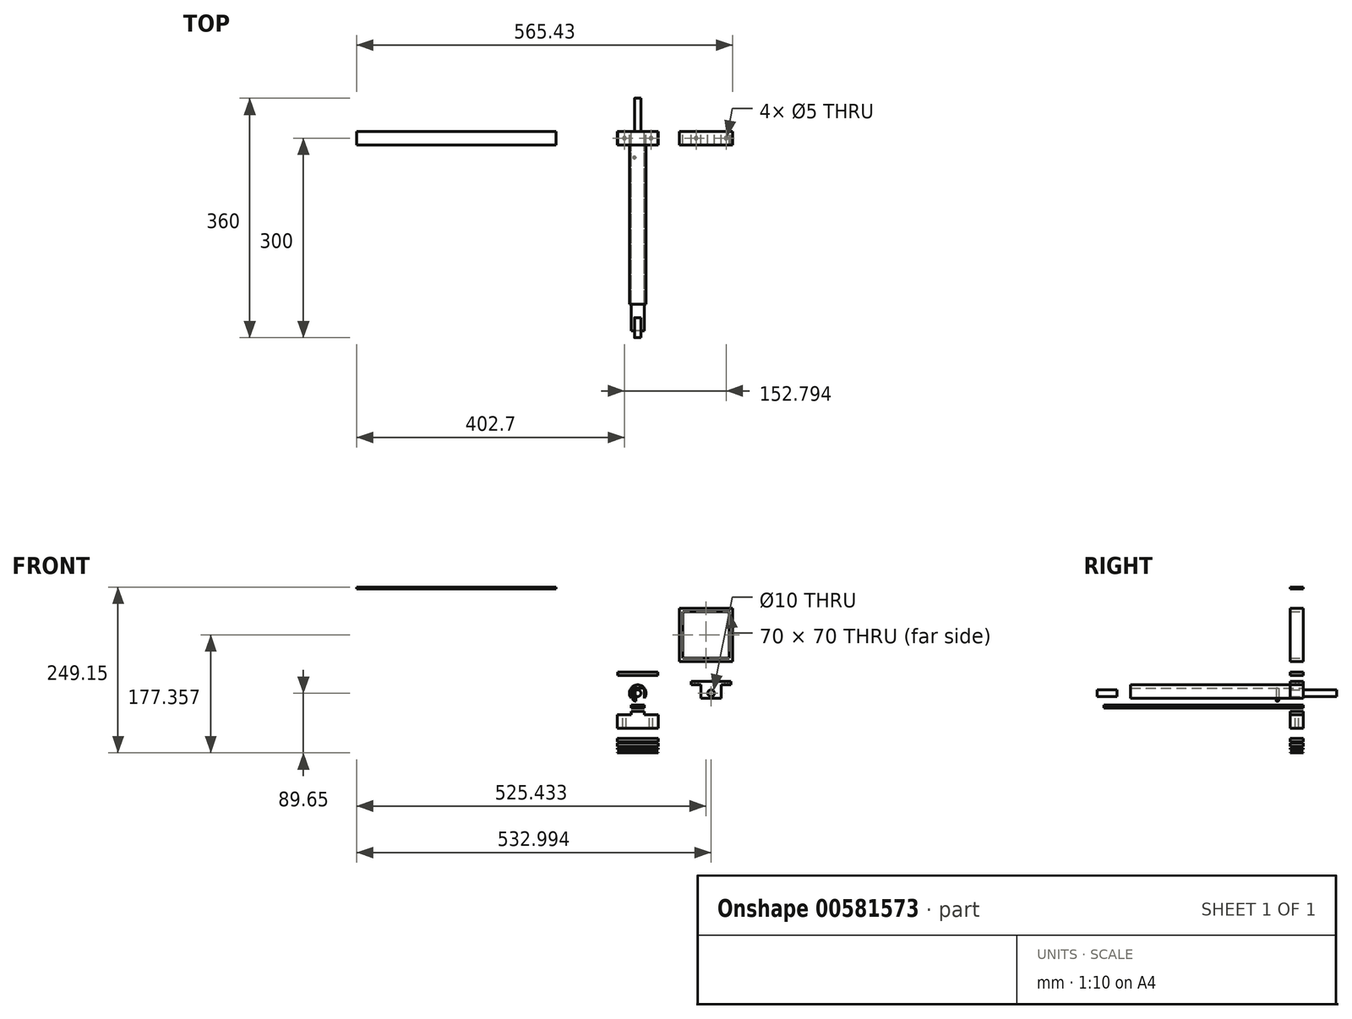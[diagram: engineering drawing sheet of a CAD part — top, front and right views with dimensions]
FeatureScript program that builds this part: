
annotation { "Feature Type Name" : "Feature", "Feature Type Description" : "" }
export const myFeature = defineFeature(function(context is Context, id is Id, definition is map)
    precondition{}
    {
        {
            var Q0;
            Q0=qCreatedBy(makeId("Front.planeOp"),FACE);
            var sketch = newSketch(context, id + "F0", { "sketchPlane" : qUnion([Q0])});
            skCircle(sketch, "E0", {"center": v(0, 0) * mm, "radius": 12.5 * mm});
            skCircle(sketch, "E1", {"center": v(110.3, 0) * mm, "radius": 5 * mm});
            skLineSegment(sketch, "E2.bottom", {"start": v(-30, 31.74) * mm, "end": v(30, 31.74) * mm});
            skLineSegment(sketch, "E2.top", {"start": v(-30, 26.74) * mm, "end": v(30, 26.74) * mm});
            skLineSegment(sketch, "E2.left", {"start": v(-30, 31.74) * mm, "end": v(-30, 26.74) * mm});
            skLineSegment(sketch, "E2.right", {"start": v(30, 31.74) * mm, "end": v(30, 26.74) * mm});
            skPoint(sketch, "E2.middle", {"position": v(0, 29.24) * mm});
            skLineSegment(sketch, "E3", {"start": v(110.3, 10) * mm, "end": v(110.3, -10) * mm, "construction": true});
            skCircle(sketch, "E4", {"center": v(110.3, 0) * mm, "radius": 12.5 * mm, "construction": true});
            skLineSegment(sketch, "E5", {"start": v(97.8, 0) * mm, "end": v(122.8, 0) * mm, "construction": true});
            skLineSegment(sketch, "E6", {"start": v(110.3, 12.5) * mm, "end": v(79.29, 12.5) * mm, "construction": true});
            skLineSegment(sketch, "E7", {"start": v(110.3, 5) * mm, "end": v(79.29, 5) * mm, "construction": true});
            skLineSegment(sketch, "E8", {"start": v(110.3, -5) * mm, "end": v(79.29, -5) * mm, "construction": true});
            skLineSegment(sketch, "E9", {"start": v(110.3, -12.5) * mm, "end": v(79.29, -12.5) * mm, "construction": true});
            skLineSegment(sketch, "E10", {"start": v(110.3, -7.5) * mm, "end": v(125.3, -7.5) * mm});
            skLineSegment(sketch, "E11", {"start": v(110.3, 17.5) * mm, "end": v(140.3, 17.5) * mm});
            skLineSegment(sketch, "E12", {"start": v(125.3, 12.5) * mm, "end": v(140.3, 12.5) * mm});
            skLineSegment(sketch, "E13", {"start": v(125.3, -7.5) * mm, "end": v(125.3, 12.5) * mm});
            skLineSegment(sketch, "E14", {"start": v(140.3, 17.5) * mm, "end": v(140.3, 12.5) * mm});
            skPoint(sketch, "E15.orphan", {"position": v(110.3, 12.5) * mm});
            skLineSegment(sketch, "E16.MirrorCS", {"start": v(95.3, 12.5) * mm, "end": v(80.3, 12.5) * mm});
            skLineSegment(sketch, "E17.MirrorCS", {"start": v(80.3, 17.5) * mm, "end": v(80.3, 12.5) * mm});
            skLineSegment(sketch, "E18.MirrorCS", {"start": v(110.3, 17.5) * mm, "end": v(80.3, 17.5) * mm});
            skLineSegment(sketch, "E19.MirrorCS", {"start": v(95.3, -7.5) * mm, "end": v(95.3, 12.5) * mm});
            skLineSegment(sketch, "E20.MirrorCS", {"start": v(110.3, -7.5) * mm, "end": v(95.3, -7.5) * mm});
            skLineSegment(sketch, "E21.top", {"start": v(0, -27.58) * mm, "end": v(10, -27.58) * mm});
            skLineSegment(sketch, "E22", {"start": v(10.93, -32.58) * mm, "end": v(30.93, -32.58) * mm});
            skLineSegment(sketch, "E23", {"start": v(30.93, -32.58) * mm, "end": v(30.93, -52.58) * mm});
            skLineSegment(sketch, "E24", {"start": v(30.93, -52.58) * mm, "end": v(0, -52.58) * mm});
            skLineSegment(sketch, "E25.MirrorCS", {"start": v(0, -27.58) * mm, "end": v(-10, -27.58) * mm});
            skLineSegment(sketch, "E26.MirrorCS", {"start": v(-10.93, -32.58) * mm, "end": v(-30.93, -32.58) * mm});
            skLineSegment(sketch, "E27.MirrorCS", {"start": v(-30.93, -32.58) * mm, "end": v(-30.93, -52.58) * mm});
            skLineSegment(sketch, "E28.MirrorCS", {"start": v(-30.93, -52.58) * mm, "end": v(0, -52.58) * mm});
            skLineSegment(sketch, "E29", {"start": v(0, -22.52) * mm, "end": v(10, -22.52) * mm});
            skLineSegment(sketch, "E30", {"start": v(10, -22.52) * mm, "end": v(10, -17.52) * mm});
            skLineSegment(sketch, "E31", {"start": v(10, -17.52) * mm, "end": v(0, -17.52) * mm});
            skLineSegment(sketch, "E32.MirrorCS", {"start": v(-10, -17.52) * mm, "end": v(0, -17.52) * mm});
            skLineSegment(sketch, "E33.MirrorCS", {"start": v(0, -22.52) * mm, "end": v(-10, -22.52) * mm});
            skLineSegment(sketch, "E34.MirrorCS", {"start": v(-10, -22.52) * mm, "end": v(-10, -17.52) * mm});
            skLineSegment(sketch, "E35.bottom", {"start": v(137.73, 52.7) * mm, "end": v(67.73, 52.7) * mm});
            skLineSegment(sketch, "E35.top", {"start": v(137.73, 122.7) * mm, "end": v(67.73, 122.7) * mm});
            skLineSegment(sketch, "E35.left", {"start": v(137.73, 52.7) * mm, "end": v(137.73, 122.7) * mm});
            skLineSegment(sketch, "E35.right", {"start": v(67.73, 52.7) * mm, "end": v(67.73, 122.7) * mm});
            skPoint(sketch, "E35.middle", {"position": v(102.73, 87.7) * mm});
            skLineSegment(sketch, "E36.bottom", {"start": v(62.73, 127.7) * mm, "end": v(142.73, 127.7) * mm});
            skLineSegment(sketch, "E36.top", {"start": v(62.73, 47.7) * mm, "end": v(142.73, 47.7) * mm});
            skLineSegment(sketch, "E36.left", {"start": v(62.73, 127.7) * mm, "end": v(62.73, 47.7) * mm});
            skLineSegment(sketch, "E36.right", {"start": v(142.73, 127.7) * mm, "end": v(142.73, 47.7) * mm});
            skLineSegment(sketch, "E37.bottom", {"start": v(-30.93, -79.86) * mm, "end": v(30.93, -79.86) * mm});
            skLineSegment(sketch, "E37.top", {"start": v(-30.93, -74.86) * mm, "end": v(30.93, -74.86) * mm});
            skLineSegment(sketch, "E37.left", {"start": v(-30.93, -79.86) * mm, "end": v(-30.93, -74.86) * mm});
            skLineSegment(sketch, "E37.right", {"start": v(30.93, -79.86) * mm, "end": v(30.93, -74.86) * mm});
            skLineSegment(sketch, "E38.MirrorCS", {"start": v(-30.74, -88.65) * mm, "end": v(31.12, -88.65) * mm});
            skLineSegment(sketch, "E39.MirrorCS", {"start": v(-30.74, -89.65) * mm, "end": v(31.12, -89.65) * mm});
            skLineSegment(sketch, "E40", {"start": v(-30.93, -82.76) * mm, "end": v(30.93, -82.76) * mm});
            skLineSegment(sketch, "E41", {"start": v(30.93, -82.76) * mm, "end": v(30.93, -84.76) * mm});
            skLineSegment(sketch, "E42", {"start": v(30.93, -84.76) * mm, "end": v(-30.93, -84.76) * mm});
            skLineSegment(sketch, "E43", {"start": v(-30.93, -84.76) * mm, "end": v(-30.93, -82.76) * mm});
            skLineSegment(sketch, "E44", {"start": v(-30.74, -88.65) * mm, "end": v(-30.74, -89.65) * mm});
            skLineSegment(sketch, "E45", {"start": v(31.12, -88.65) * mm, "end": v(31.12, -89.65) * mm});
            skLineSegment(sketch, "E46", {"start": v(-30.93, -72.74) * mm, "end": v(30.93, -72.74) * mm});
            skLineSegment(sketch, "E47", {"start": v(30.93, -72.74) * mm, "end": v(30.93, -67.74) * mm});
            skLineSegment(sketch, "E48", {"start": v(30.93, -67.74) * mm, "end": v(-30.93, -67.74) * mm});
            skLineSegment(sketch, "E49", {"start": v(-30.93, -67.74) * mm, "end": v(-30.93, -72.74) * mm});
            skLineSegment(sketch, "E50", {"start": v(-10, -27.58) * mm, "end": v(-10, -32.58) * mm});
            skLineSegment(sketch, "E51", {"start": v(-10, -32.58) * mm, "end": v(-10.93, -32.58) * mm});
            skPoint(sketch, "E52.MirrorCS.end.orphan", {"position": v(-10, -27.58) * mm});
            skPoint(sketch, "E52.MirrorCS.start.orphan", {"position": v(-10.93, -32.58) * mm});
            skLineSegment(sketch, "E53", {"start": v(10, -27.58) * mm, "end": v(10, -32.58) * mm});
            skLineSegment(sketch, "E54", {"start": v(10, -32.58) * mm, "end": v(10.93, -32.58) * mm});
            skLineSegment(sketch, "E55.left", {"start": v(194.47, 95.4) * mm, "end": v(194.47, 97.9) * mm});
            skLineSegment(sketch, "E56.bottom", {"start": v(-122.7, 157) * mm, "end": v(-422.7, 157) * mm});
            skLineSegment(sketch, "E56.top", {"start": v(-122.7, 159.5) * mm, "end": v(-422.7, 159.5) * mm});
            skLineSegment(sketch, "E56.left", {"start": v(-122.7, 157) * mm, "end": v(-122.7, 159.5) * mm});
            skLineSegment(sketch, "E56.right", {"start": v(-422.7, 157) * mm, "end": v(-422.7, 159.5) * mm});
            skLineSegment(sketch, "E57", {"start": v(-272.7, 150) * mm, "end": v(-272.7, 153.49) * mm, "construction": true});
            skPoint(sketch, "E57.startSnap0", {"position": v(-272.7, 157) * mm});
            skSolve(sketch);
        }
        {
            var Q0;
            Q0=makeQuery(id+"F0.imprint","IMPRINT",FACE,{"disambiguationData":[TD([[makeQuery(id+"F0.imprint","IMPRINT",EDGE,{"derivedFrom":sQuery(id+"F0.wireOp",EDGE,"E1")}),-1.0]])]});
            var Q1;
            Q1=makeQuery(id+"F0.imprint","IMPRINT",FACE,{"disambiguationData":[TD([[makeQuery(id+"F0.imprint","IMPRINT",EDGE,{"derivedFrom":sQuery(id+"F0.wireOp",EDGE,"E2.bottom")}),-1.0]])]});
            var Q2;
            Q2=makeQuery(id+"F0.imprint","IMPRINT",FACE,{"disambiguationData":[TD([[makeQuery(id+"F0.imprint","IMPRINT",EDGE,{"derivedFrom":sQuery(id+"F0.wireOp",EDGE,"E21.top")}),-1.0]])]});
            var Q3;
            Q3=makeQuery(id+"F0.imprint","IMPRINT",FACE,{"disambiguationData":[TD([[makeQuery(id+"F0.imprint","IMPRINT",EDGE,{"derivedFrom":sQuery(id+"F0.wireOp",EDGE,"E35.bottom")}),1.0]])]});
            var Q4;
            Q4=makeQuery(id+"F0.imprint","IMPRINT",FACE,{"disambiguationData":[TD([[makeQuery(id+"F0.imprint","IMPRINT",EDGE,{"derivedFrom":sQuery(id+"F0.wireOp",EDGE,"E37.bottom")}),1.0]])]});
            var Q5;
            Q5=makeQuery(id+"F0.imprint","IMPRINT",FACE,{"disambiguationData":[TD([[makeQuery(id+"F0.imprint","IMPRINT",EDGE,{"derivedFrom":sQuery(id+"F0.wireOp",EDGE,"E38.MirrorCS")}),-1.0]])]});
            var Q6;
            Q6=makeQuery(id+"F0.imprint","IMPRINT",FACE,{"disambiguationData":[TD([[makeQuery(id+"F0.imprint","IMPRINT",EDGE,{"derivedFrom":sQuery(id+"F0.wireOp",EDGE,"E40")}),-1.0]])]});
            var Q7;
            Q7=makeQuery(id+"F0.imprint","IMPRINT",FACE,{"disambiguationData":[TD([[makeQuery(id+"F0.imprint","IMPRINT",EDGE,{"derivedFrom":sQuery(id+"F0.wireOp",EDGE,"E46")}),1.0]])]});
            var Q8;
            {var subQ5=sQuery(id+"F0.wireOp",EDGE,"E55.right");Q8=makeQuery(id+"F0.imprint","IMPRINT",FACE,{"disambiguationData":[TD([[makeQuery(id+"F0.imprint","IMPRINT",EDGE,{"derivedFrom":subQ5}),-1.0]])]});}
            var Q9;
            Q9=makeQuery(id+"F0.imprint","IMPRINT",FACE,{"disambiguationData":[TD([[makeQuery(id+"F0.imprint","IMPRINT",EDGE,{"derivedFrom":sQuery(id+"F0.wireOp",EDGE,"E56.bottom")}),-1.0]])]});
            extrude(context, id + "F1", {"entities" : qUnion([Q0, Q1, Q2, Q3, Q4, Q5, Q6, Q7, Q8, Q9]), "depth" : 20 * mm, "offsetDistance" : 25 * mm});
        }
        {
            var Q0;
            Q0=makeQuery(id+"F0.imprint","IMPRINT",FACE,{"disambiguationData":[TD([[makeQuery(id+"F0.imprint","IMPRINT",EDGE,{"derivedFrom":sQuery(id+"F0.wireOp",EDGE,"E0")}),1.0]])]});
            extrude(context, id + "F2", {"entities" : qUnion([Q0]), "depth" : 260 * mm, "offsetDistance" : 25 * mm});
        }
        {
            var Q0;
            Q0=makeQuery(id+"F2.opExtrude","CAP_FACE",FACE,{"disambiguationData":[OSD([sQuery(id+"F0.wireOp",EDGE,"E0")])],"isStart":false});
            var sketch = newSketch(context, id + "F3", { "sketchPlane" : qUnion([Q0])});
            skCircle(sketch, "E58", {"center": v(0, 0) * mm, "radius": 5 * mm});
            skSolve(sketch);
        }
        {
            var Q0;
            Q0=makeQuery(id+"F3.imprint","IMPRINT",FACE,{"disambiguationData":[TD([[makeQuery(id+"F3.imprint","IMPRINT",EDGE,{"derivedFrom":sQuery(id+"F3.wireOp",EDGE,"E58")}),1.0]])]});
            extrude(context, id + "F4", {"entities" : qUnion([Q0]), "operationType" : NewBodyOperationType.ADD, "depth" : 50 * mm, "offsetDistance" : 25 * mm});
        }
        {
            var Q0;
            Q0=makeQuery(id+"F0.imprint","IMPRINT",FACE,{"disambiguationData":[TD([[makeQuery(id+"F0.imprint","IMPRINT",EDGE,{"derivedFrom":sQuery(id+"F0.wireOp",EDGE,"E29")}),1.0]])]});
            extrude(context, id + "F5", {"entities" : qUnion([Q0]), "depth" : 300 * mm, "offsetDistance" : 25 * mm});
        }
        {
            var Q0;
            Q0=makeQuery(id+"F1.opExtrude","SWEPT_FACE",FACE,{"disambiguationData":[OSD([sQuery(id+"F0.wireOp",EDGE,"E26.MirrorCS")])]});
            var sketch = newSketch(context, id + "F6", { "sketchPlane" : qUnion([Q0])});
            skCircle(sketch, "E59", {"center": v(-20, -10) * mm, "radius": 2.5 * mm});
            skSolve(sketch);
        }
        {
            var Q0;
            Q0=makeQuery(id+"F1.opExtrude","SWEPT_FACE",FACE,{"disambiguationData":[OSD([sQuery(id+"F0.wireOp",EDGE,"E22")])]});
            var sketch = newSketch(context, id + "F7", { "sketchPlane" : qUnion([Q0])});
            skCircle(sketch, "E60", {"center": v(20, -10) * mm, "radius": 2.5 * mm});
            skSolve(sketch);
        }
        {
            var Q0;
            Q0=makeQuery(id+"F6.imprint","IMPRINT",FACE,{"disambiguationData":[TD([[makeQuery(id+"F6.imprint","IMPRINT",EDGE,{"derivedFrom":sQuery(id+"F6.wireOp",EDGE,"E59")}),1.0]])]});
            var Q1;
            Q1=makeQuery(id+"F7.imprint","IMPRINT",FACE,{"disambiguationData":[TD([[makeQuery(id+"F7.imprint","IMPRINT",EDGE,{"derivedFrom":sQuery(id+"F7.wireOp",EDGE,"E60")}),1.0]])]});
            extrude(context, id + "F8", {"entities" : qUnion([Q0, Q1]), "operationType" : NewBodyOperationType.REMOVE, "oppositeDirection" : true, "depth" : 25 * mm, "offsetDistance" : 25 * mm});
        }
        {
            var Q0;
            Q0=makeQuery(id+"F1.opExtrude","SWEPT_FACE",FACE,{"disambiguationData":[OSD([sQuery(id+"F0.wireOp",EDGE,"E12")])]});
            var sketch = newSketch(context, id + "F9", { "sketchPlane" : qUnion([Q0])});
            skCircle(sketch, "E61", {"center": v(132.8, 10) * mm, "radius": 2.5 * mm});
            skPoint(sketch, "E61.centerSnap0", {"position": v(132.8, 20) * mm});
            skPoint(sketch, "E61.centerSnap1", {"position": v(125.3, 10) * mm});
            skSolve(sketch);
        }
        {
            var Q0;
            Q0=makeQuery(id+"F1.opExtrude","SWEPT_FACE",FACE,{"disambiguationData":[OSD([sQuery(id+"F0.wireOp",EDGE,"E16.MirrorCS")])]});
            var sketch = newSketch(context, id + "F10", { "sketchPlane" : qUnion([Q0])});
            skCircle(sketch, "E62", {"center": v(87.8, 10) * mm, "radius": 2.5 * mm});
            skPoint(sketch, "E62.centerSnap0", {"position": v(80.3, 10) * mm});
            skPoint(sketch, "E62.centerSnap1", {"position": v(87.8, 20) * mm});
            skSolve(sketch);
        }
        {
            var Q0;
            Q0=makeQuery(id+"F10.imprint","IMPRINT",FACE,{"disambiguationData":[TD([[makeQuery(id+"F10.imprint","IMPRINT",EDGE,{"derivedFrom":sQuery(id+"F10.wireOp",EDGE,"E62")}),1.0]])]});
            var Q1;
            Q1=makeQuery(id+"F9.imprint","IMPRINT",FACE,{"disambiguationData":[TD([[makeQuery(id+"F9.imprint","IMPRINT",EDGE,{"derivedFrom":sQuery(id+"F9.wireOp",EDGE,"E61")}),1.0]])]});
            extrude(context, id + "F11", {"entities" : qUnion([Q0, Q1]), "operationType" : NewBodyOperationType.REMOVE, "oppositeDirection" : true, "depth" : 25 * mm, "offsetDistance" : 25 * mm});
        }
        {
            var Q0;
            Q0=makeQuery(id+"F5.opExtrude","SWEPT_FACE",FACE,{"disambiguationData":[OSD([sQuery(id+"F0.wireOp",EDGE,"E31"),sQuery(id+"F0.wireOp",EDGE,"E32.MirrorCS")])]});
            var sketch = newSketch(context, id + "F12", { "sketchPlane" : qUnion([Q0])});
            skLineSegment(sketch, "E63", {"start": v(-10, -280) * mm, "end": v(10, -280) * mm});
            skCircle(sketch, "E64", {"center": v(5, -39.13) * mm, "radius": 1.93 * mm});
            skPoint(sketch, "E65.orphan", {"position": v(0, -300) * mm});
            skCircle(sketch, "E66.MirrorC", {"center": v(-5, -39.13) * mm, "radius": 1.93 * mm});
            skSolve(sketch);
        }
        {
            var Q0;
            Q0=makeQuery(id+"F12.imprint","IMPRINT",FACE,{"disambiguationData":[TD([[makeQuery(id+"F12.imprint","IMPRINT",EDGE,{"derivedFrom":sQuery(id+"F12.wireOp",EDGE,"E66.MirrorC")}),-1.0]])]});
            var Q1;
            Q1=makeQuery(id+"F12.imprint","IMPRINT",FACE,{"disambiguationData":[TD([[makeQuery(id+"F12.imprint","IMPRINT",EDGE,{"derivedFrom":sQuery(id+"F12.wireOp",EDGE,"E64")}),1.0]])]});
            extrude(context, id + "F13", {"entities" : qUnion([Q0, Q1]), "operationType" : NewBodyOperationType.REMOVE, "depth" : 25 * mm, "offsetDistance" : 25 * mm});
        }
        {
            var Q0;
            Q0=makeQuery(id+"F1.opExtrude","SWEPT_FACE",FACE,{"disambiguationData":[OSD([sQuery(id+"F0.wireOp",EDGE,"E56.bottom")])]});
            var sketch = newSketch(context, id + "F14", { "sketchPlane" : qUnion([Q0])});
            skLineSegment(sketch, "E67", {"start": v(-402.7, 0) * mm, "end": v(-402.7, 20) * mm});
            skLineSegment(sketch, "E68", {"start": v(-142.7, 0) * mm, "end": v(-142.7, 20) * mm});
            skLineSegment(sketch, "E69", {"start": v(82.73, 0) * mm, "end": v(82.73, 20) * mm});
            skLineSegment(sketch, "E70", {"start": v(122.73, 0) * mm, "end": v(122.73, 20) * mm});
            skSolve(sketch);
        }
        {
            var Q0;
            Q0=makeQuery(id+"F1.opExtrude","SWEPT_FACE",FACE,{"disambiguationData":[OSD([sQuery(id+"F0.wireOp",EDGE,"E36.bottom")])]});
            var sketch = newSketch(context, id + "F15", { "sketchPlane" : qUnion([Q0])});
            skLineSegment(sketch, "E71", {"start": v(82.73, 0) * mm, "end": v(82.73, -20) * mm});
            skLineSegment(sketch, "E72", {"start": v(122.73, -20) * mm, "end": v(122.73, 0) * mm});
            skSolve(sketch);
        }
        {
            var Q0;
            Q0=makeQuery(id+"F1.opExtrude","SWEPT_FACE",FACE,{"disambiguationData":[OSD([sQuery(id+"F0.wireOp",EDGE,"E36.top")])]});
            var sketch = newSketch(context, id + "F16", { "sketchPlane" : qUnion([Q0])});
            skLineSegment(sketch, "E73", {"start": v(122.73, 20) * mm, "end": v(122.73, 0) * mm});
            skLineSegment(sketch, "E74", {"start": v(82.73, 20) * mm, "end": v(82.73, 0) * mm});
            skSolve(sketch);
        }
        {
            var Q0;
            Q0=makeQuery(id+"F2.opExtrude","CAP_FACE",FACE,{"disambiguationData":[OSD([sQuery(id+"F0.wireOp",EDGE,"E0")])],"isStart":true});
            var sketch = newSketch(context, id + "F17", { "sketchPlane" : qUnion([Q0])});
            skCircle(sketch, "E75", {"center": v(0, 0) * mm, "radius": 5 * mm});
            skSolve(sketch);
        }
        {
            var Q0;
            Q0=qSketchRegion(id+"F17",true);
            extrude(context, id + "F18", {"entities" : qUnion([Q0]), "operationType" : NewBodyOperationType.ADD, "depth" : 50 * mm, "offsetDistance" : 25 * mm});
        }
    });
